# Revit family: LG_Single_R32_Indoor_Console_9-12kBtu_NA
name_source: partatom
category: Mechanical Equipment
units: mm (PartAtom-declared; Revit-internal decimal feet)

## family parameters
Always vertical = Yes
Cut with Voids When Loaded = No
Part Type = Normal
Room Calculation Point = No
Round Connector Dimension = Use Radius
Shared = No
Work Plane-Based = No

## types (2) — shared parameters
Chassis name = QA
Condensate Drain Connection Diameter = 17 mm
Condensate Drain Connection Offset Top = 32 mm  [stored 0.104987 ft]
Condensate Drain Connection Offset back = 34 mm
Condensate Drain Connection Radius = 9 mm  [stored 0.0295276 ft]
Dimensions (WxHxD)(inch) = 27-9/16 x 23-5/8 x 8-9/32
Dimensions (WxHxD)(mm) = 700 x 600 x 210
Fan Motor Output (W) = 48
Fan Motor Type = -
Fan Type = Turbo
Height = 600 mm
Height offset bottom = 86 mm  [stored 0.282152 ft]
Height offset mid = 74 mm  [stored 0.242782 ft]
Height offset top = 55 mm  [stored 0.180446 ft]
Length = 700 mm  [stored 2.29659 ft]
Length offset front = 69 mm  [stored 0.226378 ft]
Length offset left = 20 mm  [stored 0.0656168 ft]
Manufacturer = LG Electronics
Net Weight (kg) = 16.2
Net Weight (lbs) = 35.7
Pipe Connection_Drain Side (inch) = 21/32
Pipe Connection_Drain Side (mm) = 17
Pipe Connection_Gas Side (inch) = 3/8
Pipe Connection_Gas Side (mm) = 9.52
Pipe Connection_Liquid Side (inch) = 1/4
Pipe Connection_Liquid Side (mm) = 6.35
Power Supply (Ph_V_Hz) = 1, 208-230, 60
Power and Communication Cable = -
Refrigerant Gas Connection Diameter = 10 mm
Refrigerant Gas Connection Offset Top = 52 mm
Refrigerant Gas Connection Offset back = 44 mm  [stored 0.144357 ft]
Refrigerant Gas Connection Radius = 5 mm  [stored 0.0164042 ft]
Refrigerant Liquid Connection Diameter = 6 mm
Refrigerant Liquid Connection Offset Top = 60 mm  [stored 0.19685 ft]
Refrigerant Liquid Connection Offset back = 34 mm
Refrigerant Liquid Connection Radius = 3 mm  [stored 0.00984252 ft]
Refrigerant Type = R32
Sound Power Level (dB(A)) = -
Type = Console
URL = https://lghvac.com
Width = 210 mm  [stored 0.688976 ft]
Width offset back = 54 mm  [stored 0.177165 ft]
Width offset grill back = 50 mm  [stored 0.164042 ft]
zero-valued in all types: Default Elevation

## per-type parameters (varying)
| type | Air Flow Rate (H/M/L)(CFM) | Air Flow Rate (H/M/L)(CMM) | Cooling Capacity (Btu/h) | Cooling Capacity (kW) | Heating Capacity (Btu/h) | Heating Capacity (kW) | Model name (Factory) | Power Input (Cooling)(W) | Power Input (Heating)(W) | Running Current (A) | Sound Pressure Level Cooling(dB) | Sound Pressure Level Heating(dB) |
| KNUQB091A | 318(MAX) / 300 / 237 / 177 | 9.0(MAX) / 8.5 / 6.7 / 5.0 | 9000 | 2.6 | 10100 | 3.0 | KUSXB091A | 680.00 | 760.000 | 2.96 | 38 / 32 / 27 | 38 / 32 / 27 |
| KNUQB121A | 353(MAX) / 318 / 244 / 184 | 10.0(MAX) / 9.0 / 6.9 / 5.2 | 10200 | 3 | 13000 | 3.8 | KUSXB121A | 780.00 | 1,060.000 | 3.39 | 39 / 32 / 27 | 39 / 32 / 27 |

note: column(s) folded — value = type name in every type: Model name (Buyer)

note: [stored X ft] marks values corroborated as IEEE doubles in the binary element streams (Revit-internal decimal feet)

## geometry (parser evidence)
native form markers: Sweep x2
no freeform markers — native parametric forms only
